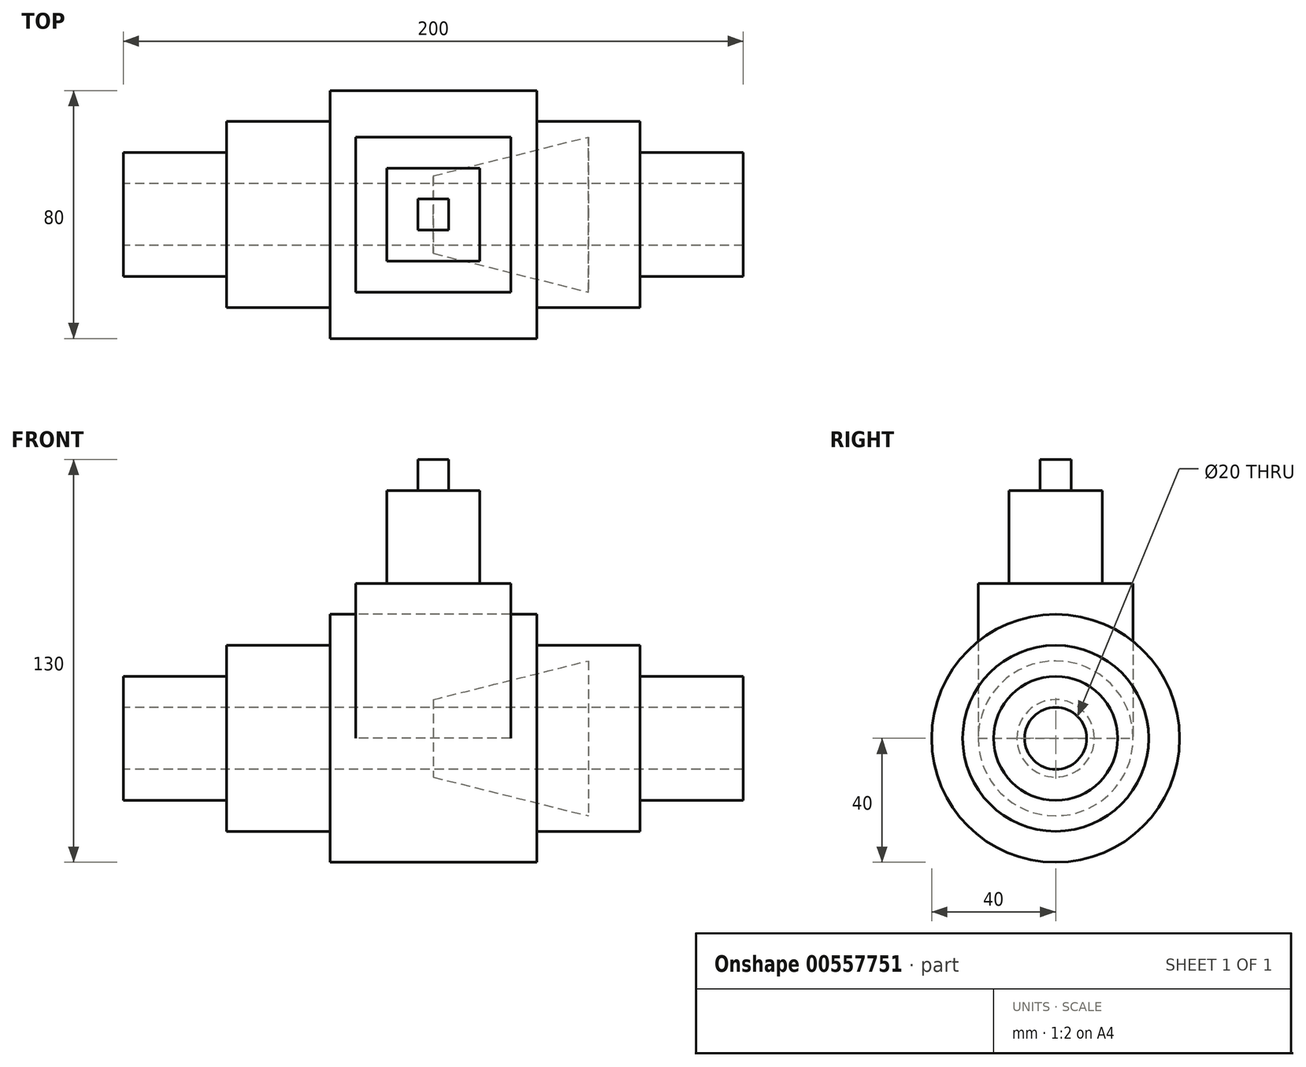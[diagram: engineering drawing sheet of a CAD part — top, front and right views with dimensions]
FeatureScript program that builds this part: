
annotation { "Feature Type Name" : "Feature", "Feature Type Description" : "" }
export const myFeature = defineFeature(function(context is Context, id is Id, definition is map)
    precondition{}
    {
        {
            var Q0;
            Q0=qCreatedBy(makeId("Top.planeOp"),FACE);
            var sketch = newSketch(context, id + "F0", { "sketchPlane" : qUnion([Q0])});
            skLineSegment(sketch, "E0.bottom", {"start": v(25, -25) * mm, "end": v(-25, -25) * mm});
            skLineSegment(sketch, "E0.top", {"start": v(25, 25) * mm, "end": v(-25, 25) * mm});
            skLineSegment(sketch, "E0.left", {"start": v(25, -25) * mm, "end": v(25, 25) * mm});
            skLineSegment(sketch, "E0.right", {"start": v(-25, -25) * mm, "end": v(-25, 25) * mm});
            skPoint(sketch, "E0.middle", {"position": v(0, 0) * mm});
            skSolve(sketch);
        }
        {
            var Q0;
            Q0 = qSketchRegion(id + "F0", true);
            extrude(context, id + "F1", {"entities" : qUnion([Q0]), "depth" : 50 * mm, "offsetDistance" : 25 * mm});
        }
        {
            var Q0;
            Q0=qCreatedBy(makeId("Top.planeOp"),FACE);
            var sketch = newSketch(context, id + "F2", { "sketchPlane" : qUnion([Q0])});
            skLineSegment(sketch, "E1.bottom", {"start": v(25, -25) * mm, "end": v(-25, -25) * mm});
            skLineSegment(sketch, "E1.top", {"start": v(25, 25) * mm, "end": v(-25, 25) * mm});
            skLineSegment(sketch, "E1.left", {"start": v(25, -25) * mm, "end": v(25, 25) * mm});
            skLineSegment(sketch, "E1.right", {"start": v(-25, -25) * mm, "end": v(-25, 25) * mm});
            skPoint(sketch, "E1.middle", {"position": v(0, 0) * mm});
            skSolve(sketch);
        }
        {
            var Q0;
            Q0=makeQuery(id+"F2.imprint","IMPRINT",FACE,{"disambiguationData":[TD([[makeQuery(id+"F2.imprint","IMPRINT",EDGE,{"derivedFrom":sQuery(id+"F2.wireOp",EDGE,"E1.bottom")}),-1.0]])]});
            extrude(context, id + "F3", {"entities" : qUnion([Q0]), "depth" : 50 * mm, "offsetDistance" : 25 * mm});
        }
        {
            var Q0;
            Q0=makeQuery(id+"F3.opExtrude","CAP_FACE",FACE,{"disambiguationData":[OSD([sQuery(id+"F2.wireOp",EDGE,"E1.bottom"),sQuery(id+"F2.wireOp",EDGE,"E1.top"),sQuery(id+"F2.wireOp",EDGE,"E1.left"),sQuery(id+"F2.wireOp",EDGE,"E1.right")])],"isStart":false});
            var sketch = newSketch(context, id + "F4", { "sketchPlane" : qUnion([Q0])});
            skLineSegment(sketch, "E2.bottom", {"start": v(15, -15) * mm, "end": v(-15, -15) * mm});
            skLineSegment(sketch, "E2.top", {"start": v(15, 15) * mm, "end": v(-15, 15) * mm});
            skLineSegment(sketch, "E2.left", {"start": v(15, -15) * mm, "end": v(15, 15) * mm});
            skLineSegment(sketch, "E2.right", {"start": v(-15, -15) * mm, "end": v(-15, 15) * mm});
            skPoint(sketch, "E2.middle", {"position": v(0, 0) * mm});
            skSolve(sketch);
        }
        {
            var Q0;
            Q0=makeQuery(id+"F4.imprint","IMPRINT",FACE,{"disambiguationData":[TD([[makeQuery(id+"F4.imprint","IMPRINT",EDGE,{"derivedFrom":sQuery(id+"F4.wireOp",EDGE,"E2.bottom")}),-1.0]])]});
            extrude(context, id + "F5", {"entities" : qUnion([Q0]), "operationType" : NewBodyOperationType.ADD, "depth" : 30 * mm, "offsetDistance" : 25 * mm});
        }
        {
            var Q0;
            Q0=makeQuery(id+"F5.opExtrude","CAP_FACE",FACE,{"disambiguationData":[OSD([sQuery(id+"F4.wireOp",EDGE,"E2.bottom"),sQuery(id+"F4.wireOp",EDGE,"E2.top"),sQuery(id+"F4.wireOp",EDGE,"E2.left"),sQuery(id+"F4.wireOp",EDGE,"E2.right")])],"isStart":false});
            var sketch = newSketch(context, id + "F6", { "sketchPlane" : qUnion([Q0])});
            skLineSegment(sketch, "E3.bottom", {"start": v(5, -5) * mm, "end": v(-5, -5) * mm});
            skLineSegment(sketch, "E3.top", {"start": v(5, 5) * mm, "end": v(-5, 5) * mm});
            skLineSegment(sketch, "E3.left", {"start": v(5, -5) * mm, "end": v(5, 5) * mm});
            skLineSegment(sketch, "E3.right", {"start": v(-5, -5) * mm, "end": v(-5, 5) * mm});
            skPoint(sketch, "E3.middle", {"position": v(0, 0) * mm});
            skSolve(sketch);
        }
        {
            var Q0;
            Q0=makeQuery(id+"F6.imprint","IMPRINT",FACE,{"disambiguationData":[TD([[makeQuery(id+"F6.imprint","IMPRINT",EDGE,{"derivedFrom":sQuery(id+"F6.wireOp",EDGE,"E3.bottom")}),-1.0]])]});
            extrude(context, id + "F7", {"entities" : qUnion([Q0]), "operationType" : NewBodyOperationType.ADD, "depth" : 10 * mm, "offsetDistance" : 25 * mm});
        }
        {
            var Q0;
            Q0=qCreatedBy(makeId("Front.planeOp"),FACE);
            var sketch = newSketch(context, id + "F8", { "sketchPlane" : qUnion([Q0])});
            skLineSegment(sketch, "E4", {"start": v(0, 0) * mm, "end": v(0, 12.5) * mm});
            skLineSegment(sketch, "E5", {"start": v(0, 12.5) * mm, "end": v(50, 25) * mm});
            skLineSegment(sketch, "E6", {"start": v(50, 25) * mm, "end": v(50, 0) * mm});
            skLineSegment(sketch, "E7", {"start": v(50, 0) * mm, "end": v(0, 0) * mm});
            skLineSegment(sketch, "E8", {"start": v(-19.25, 0) * mm, "end": v(67.68, 0) * mm, "construction": true});
            skSolve(sketch);
        }
        {
            var Q0;
            Q0=makeQuery(id+"F8.imprint","IMPRINT",FACE,{"disambiguationData":[TD([[makeQuery(id+"F8.imprint","IMPRINT",EDGE,{"derivedFrom":sQuery(id+"F8.wireOp",EDGE,"E4")}),-1.0]])]});
            var Q1;
            Q1=sQuery(id+"F8.wireOp",EDGE,"E8");
            revolve(context, id + "F9", {"entities" : qUnion([Q0]), "axis" : qUnion([Q1]), "revolveType" : RevolveType.FULL});
        }
        {
            var Q0;
            Q0=qCreatedBy(makeId("Front.planeOp"),FACE);
            var sketch = newSketch(context, id + "F10", { "sketchPlane" : qUnion([Q0])});
            skLineSegment(sketch, "E9", {"start": v(-100, 10) * mm, "end": v(-100, 20) * mm});
            skLineSegment(sketch, "E10", {"start": v(-100, 20) * mm, "end": v(-66.67, 20) * mm});
            skLineSegment(sketch, "E11", {"start": v(-66.67, 20) * mm, "end": v(-66.67, 30) * mm});
            skLineSegment(sketch, "E12", {"start": v(-66.67, 30) * mm, "end": v(-33.33, 30) * mm});
            skLineSegment(sketch, "E13", {"start": v(-33.33, 30) * mm, "end": v(-33.33, 40) * mm});
            skLineSegment(sketch, "E14", {"start": v(-33.33, 40) * mm, "end": v(0, 40) * mm});
            skLineSegment(sketch, "E15", {"start": v(-100, 10) * mm, "end": v(0, 10) * mm});
            skLineSegment(sketch, "E16", {"start": v(-65.37, 0) * mm, "end": v(67.32, 0) * mm, "construction": true});
            skLineSegment(sketch, "E17.MirrorCS", {"start": v(33.33, 40) * mm, "end": v(0, 40) * mm});
            skLineSegment(sketch, "E18.MirrorCS", {"start": v(33.33, 30) * mm, "end": v(33.33, 40) * mm});
            skLineSegment(sketch, "E19.MirrorCS", {"start": v(66.67, 30) * mm, "end": v(33.33, 30) * mm});
            skLineSegment(sketch, "E20.MirrorCS", {"start": v(66.67, 20) * mm, "end": v(66.67, 30) * mm});
            skLineSegment(sketch, "E21.MirrorCS", {"start": v(100, 10) * mm, "end": v(100, 20) * mm});
            skLineSegment(sketch, "E22.MirrorCS", {"start": v(100, 10) * mm, "end": v(0, 10) * mm});
            skLineSegment(sketch, "E23.MirrorCS", {"start": v(100, 20) * mm, "end": v(66.67, 20) * mm});
            skSolve(sketch);
        }
        {
            var Q0;
            Q0=makeQuery(id+"F10.imprint","IMPRINT",FACE,{"disambiguationData":[TD([[makeQuery(id+"F10.imprint","IMPRINT",EDGE,{"derivedFrom":sQuery(id+"F10.wireOp",EDGE,"E9")}),-1.0]])]});
            var Q1;
            Q1=sQuery(id+"F10.wireOp",EDGE,"E16");
            revolve(context, id + "F11", {"entities" : qUnion([Q0]), "axis" : qUnion([Q1]), "revolveType" : RevolveType.FULL});
        }
    });
